# Revit family: LUS-200_RFA
name_source: partatom
category: Aparatos sanitarios
units: mm (PartAtom-declared; Revit-internal decimal feet)

## family parameters
Compartido = Sí
Corte con vacíos al cargar = No
Cota de conector redondo = Diámetro de uso
Número OmniClass = 23.45.55.14
Punto de cálculo de habitación = Sí
Se basa en plano de trabajo = Sí
Siempre vertical = Sí
Tipo de pieza = Normal
Título OmniClass = Single Faucets

## types (1)
- LUS-200
    Accesorios = Llave allen 5/64".
    Características = Monomando para regadera o tina sin 
desviador con cartucho cerámico de 35mm.
Integra una caja de instalación rápida con 
nivel de profundidad, nivel de burbuja para 
nivelar en el plano horizontal y vertical, 
conexiones hembra roscadas para eliminar 
fugas de conexión. 
En caso de fuga el agua se encapsula en el 
interior de la caja de instalación y 
no se expande al muro, la caja se puede instalar de dorso contra dorso. La forma cuadrada de la caja de instalación permite cortes en ángulo recto.
    Descripción = Monomando para Regadera o Tina sin Desviador.
    Elevación por defecto = 47"
    Fabricante = HELVEX S.A. DE C.V.
    Imagen de tipo = LUS-200.PNG
    Instalación = Conexión interna de 1/2"-14 NPT para agua fría (azul). Conexión interna de 1/2"-14 NPT para agua caliente (rojo). Conexión interna de 1/2"-14 NPT de salida (negro).
    Material = Brass
    Modelo = LUS-200
    Operación = Para abrir el flujo de agua levante la palanca maneral y gire para regular la temperatura.
    Presión máxima de trabajo = 85.3 psi
    Presión mínima de trabajo = 11.4 psi
    Total Height = 5"
    Total Weidht = 4"
    URL = https://helvex.com.mx

## geometry (parser evidence)
native form markers: Sweep x3
no freeform markers — native parametric forms only
